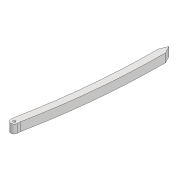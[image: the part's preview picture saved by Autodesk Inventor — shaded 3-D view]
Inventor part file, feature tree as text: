
AUTODESK INVENTOR PART (.ipt)
format: ipt  version: 2022 (Build 260153000, 153)  size: 129,024 bytes
history: native  units: mm
features: extrude x3, sketch x3, projected_geometry x2
ambient origin geometry x8: Origin, YZ Plane, XZ Plane, XY Plane, X Axis, Y Axis, Z Axis, Center Point
bodies: Solid1 (feature_tree)
feature tree (8):
  extrude  "Extrusion1"  Depth=8.0mm
  extrude  "Extrusion3"  Depth=3.0mm
  extrude  "Extrusion2"  Depth=800.0mm
  sketch  "Sketch1"  dims[d0=8.0mm d1=315.198mm]
  sketch  "Sketch3"  dims[d2=3.0mm d3=3.0mm]
  projected_geometry  "Projected Loop2"
  sketch  "Sketch4"  dims[d4=10.0mm d5=0.0mm d24=800.0mm d25=800.0mm d26=3.0mm d27=3.0mm d30=100.0mm d31=0.0mm d32=10.0mm d33=0.0mm]
  projected_geometry  "Projected Loop3"
